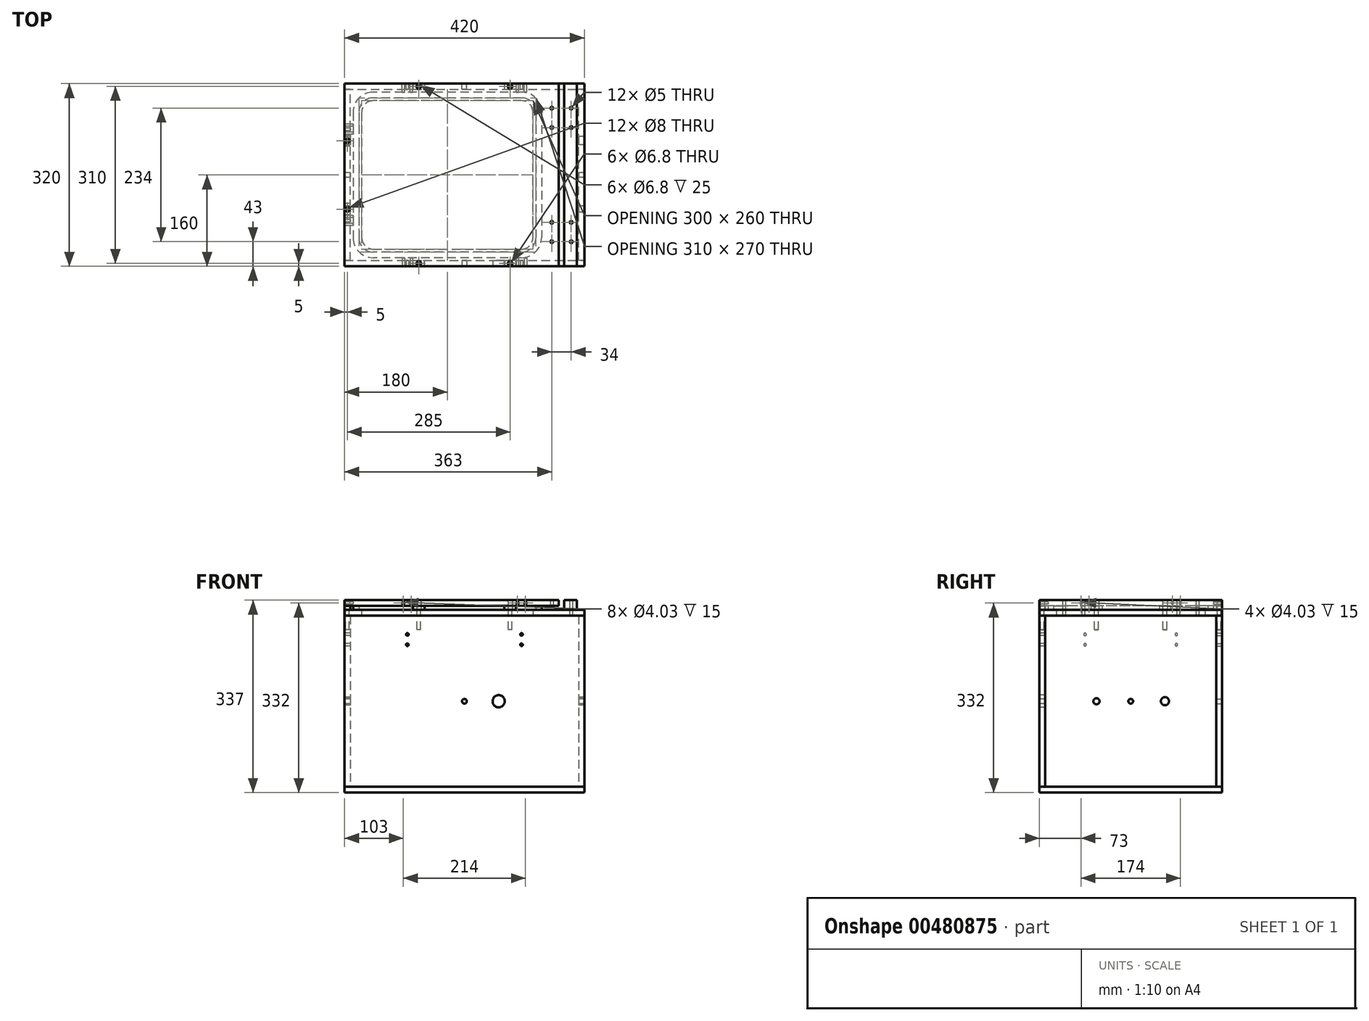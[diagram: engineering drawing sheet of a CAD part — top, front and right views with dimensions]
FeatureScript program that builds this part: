
annotation { "Feature Type Name" : "Feature", "Feature Type Description" : "" }
export const myFeature = defineFeature(function(context is Context, id is Id, definition is map)
    precondition{}
    {
        {
            var Q0;
            Q0=qCreatedBy(makeId("Top.planeOp"),FACE);
            var sketch = newSketch(context, id + "F0", { "sketchPlane" : qUnion([Q0])});
            skLineSegment(sketch, "E0.bottom", {"start": v(-210, 150) * mm, "end": v(210, 150) * mm});
            skLineSegment(sketch, "E0.top", {"start": v(-210, -150) * mm, "end": v(210, -150) * mm});
            skLineSegment(sketch, "E0.left", {"start": v(-200, 150) * mm, "end": v(-200, -150) * mm});
            skLineSegment(sketch, "E0.right", {"start": v(200, 150) * mm, "end": v(200, -150) * mm});
            skLineSegment(sketch, "E1", {"start": v(-200, 0) * mm, "end": v(200, 0) * mm, "construction": true});
            skLineSegment(sketch, "E2", {"start": v(0, -150) * mm, "end": v(0, 150) * mm, "construction": true});
            skLineSegment(sketch, "E3.0", {"start": v(210, 160) * mm, "end": v(210, -160) * mm});
            skLineSegment(sketch, "E3.1", {"start": v(-210, 160) * mm, "end": v(210, 160) * mm});
            skLineSegment(sketch, "E3.2", {"start": v(-210, 160) * mm, "end": v(-210, -160) * mm});
            skLineSegment(sketch, "E3.3", {"start": v(-210, -160) * mm, "end": v(210, -160) * mm});
            skLineSegment(sketch, "E4", {"start": v(-200, 150) * mm, "end": v(-200, 160) * mm, "construction": true});
            skLineSegment(sketch, "E5", {"start": v(-200, -150) * mm, "end": v(-200, -160) * mm, "construction": true});
            skSolve(sketch);
        }
        {
            var Q0;
            Q0=qCreatedBy(makeId("Top.planeOp"),FACE);
            cPlane(context, id + "F1", {"entities" : qUnion([Q0]), "cplaneType" : CPlaneType.OFFSET, "offset" : 150 * mm, "width" : 150 * mm, "height" : 150 * mm});
        }
        {
            var Q0;
            Q0=qCreatedBy(makeId("Top.planeOp"),FACE);
            cPlane(context, id + "F2", {"entities" : qUnion([Q0]), "cplaneType" : CPlaneType.OFFSET, "offset" : 150 * mm, "oppositeDirection" : true, "width" : 150 * mm, "height" : 150 * mm});
        }
        {
            var Q0;
            Q0=qCreatedBy(id+"F2.planeOp",FACE);
            var sketch = newSketch(context, id + "F3", { "sketchPlane" : qUnion([Q0])});
            skLineSegment(sketch, "E6.0", {"start": v(-210, 160) * mm, "end": v(-210, -160) * mm});
            skLineSegment(sketch, "E7.0", {"start": v(-210, 160) * mm, "end": v(210, 160) * mm});
            skLineSegment(sketch, "E8.0", {"start": v(-210, -160) * mm, "end": v(210, -160) * mm});
            skLineSegment(sketch, "E9.0", {"start": v(210, 160) * mm, "end": v(210, -160) * mm});
            skSolve(sketch);
        }
        {
            var Q0;
            Q0=qCreatedBy(id+"F1.planeOp",FACE);
            var sketch = newSketch(context, id + "F4", { "sketchPlane" : qUnion([Q0])});
            skLineSegment(sketch, "E10.0", {"start": v(-210, 160) * mm, "end": v(210, 160) * mm});
            skLineSegment(sketch, "E11.0", {"start": v(-210, 160) * mm, "end": v(-210, -160) * mm});
            skLineSegment(sketch, "E12.0", {"start": v(-210, -160) * mm, "end": v(210, -160) * mm});
            skLineSegment(sketch, "E13.0", {"start": v(210, 160) * mm, "end": v(210, -160) * mm});
            skSolve(sketch);
        }
        {
            var Q0;
            Q0=qCreatedBy(makeId("Right.planeOp"),FACE);
            var Q1;
            Q1=sQuery(id+"F0.wireOp",EDGE,"E0.left");
            cPlane(context, id + "F5", {"entities" : qUnion([Q0, Q1]), "cplaneType" : CPlaneType.LINE_ANGLE, "offset" : 25 * mm, "angle" : 0 * degree, "width" : 150 * mm, "height" : 150 * mm});
        }
        {
            var Q0;
            Q0=qCreatedBy(id+"F5.planeOp",FACE);
            var sketch = newSketch(context, id + "F6", { "sketchPlane" : qUnion([Q0])});
            skLineSegment(sketch, "E14.bottom", {"start": v(-160, 150) * mm, "end": v(160, 150) * mm});
            skLineSegment(sketch, "E14.top", {"start": v(-160, -150) * mm, "end": v(160, -150) * mm});
            skLineSegment(sketch, "E14.left", {"start": v(-160, 150) * mm, "end": v(-160, -150) * mm});
            skLineSegment(sketch, "E14.right", {"start": v(160, 150) * mm, "end": v(160, -150) * mm});
            skPoint(sketch, "E15.0", {"position": v(-160, 0) * mm});
            skPoint(sketch, "E16.0", {"position": v(160, 0) * mm});
            skCircle(sketch, "E17", {"center": v(0, 0) * mm, "radius": 4.17 * mm});
            skCircle(sketch, "E18", {"center": v(60, 0) * mm, "radius": 5.36 * mm});
            skCircle(sketch, "E19", {"center": v(-60, 0) * mm, "radius": 7.13 * mm});
            skSolve(sketch);
        }
        {
            var Q0;
            Q0=makeQuery(id+"F4.imprint","IMPRINT",FACE,{"disambiguationData":[TD([[makeQuery(id+"F4.imprint","IMPRINT",EDGE,{"derivedFrom":sQuery(id+"F4.wireOp",EDGE,"E11.0")}),1.0]])]});
            var sketch = newSketch(context, id + "F7", { "sketchPlane" : qUnion([Q0])});
            skLineSegment(sketch, "E20.0", {"start": v(-210, 160) * mm, "end": v(210, 160) * mm});
            skLineSegment(sketch, "E21.0", {"start": v(210, 160) * mm, "end": v(210, -160) * mm, "construction": true});
            skLineSegment(sketch, "E22.0", {"start": v(-210, -160) * mm, "end": v(210, -160) * mm});
            skLineSegment(sketch, "E23.0", {"start": v(-210, 160) * mm, "end": v(-210, -160) * mm});
            skLineSegment(sketch, "E24.bottom", {"start": v(100, 130) * mm, "end": v(-160, 130) * mm});
            skLineSegment(sketch, "E24.top", {"start": v(100, -130) * mm, "end": v(-160, -130) * mm});
            skLineSegment(sketch, "E24.left", {"start": v(120, 110) * mm, "end": v(120, -110) * mm});
            skLineSegment(sketch, "E24.right", {"start": v(-180, 110) * mm, "end": v(-180, -110) * mm});
            skPoint(sketch, "E25.visualSharp", {"position": v(120, 130) * mm});
            skArc(sketch, "E25.filletArc", {"start": v(120, 110) * mm, "mid": v(114.14, 124.14) * mm, "end": v(100, 130) * mm});
            skPoint(sketch, "E26.visualSharp", {"position": v(-180, 130) * mm});
            skArc(sketch, "E26.filletArc", {"start": v(-160, 130) * mm, "mid": v(-174.14, 124.14) * mm, "end": v(-180, 110) * mm});
            skPoint(sketch, "E27.visualSharp", {"position": v(-180, -130) * mm});
            skArc(sketch, "E27.filletArc", {"start": v(-180, -110) * mm, "mid": v(-174.14, -124.14) * mm, "end": v(-160, -130) * mm});
            skPoint(sketch, "E28.visualSharp", {"position": v(120, -130) * mm});
            skArc(sketch, "E28.filletArc", {"start": v(100, -130) * mm, "mid": v(114.14, -124.14) * mm, "end": v(120, -110) * mm});
            skLineSegment(sketch, "E29.0", {"start": v(100, 135) * mm, "end": v(-160, 135) * mm});
            skArc(sketch, "E29.1", {"start": v(125, 110) * mm, "mid": v(117.68, 127.68) * mm, "end": v(100, 135) * mm});
            skArc(sketch, "E29.2", {"start": v(-160, 135) * mm, "mid": v(-177.68, 127.68) * mm, "end": v(-185, 110) * mm});
            skLineSegment(sketch, "E29.3", {"start": v(125, 110) * mm, "end": v(125, -110) * mm});
            skLineSegment(sketch, "E29.4", {"start": v(-185, 110) * mm, "end": v(-185, -110) * mm});
            skArc(sketch, "E29.5", {"start": v(-185, -110) * mm, "mid": v(-177.68, -127.68) * mm, "end": v(-160, -135) * mm});
            skLineSegment(sketch, "E29.6", {"start": v(100, -135) * mm, "end": v(-160, -135) * mm});
            skArc(sketch, "E29.7", {"start": v(100, -135) * mm, "mid": v(117.68, -127.68) * mm, "end": v(125, -110) * mm});
            skArc(sketch, "E30.0", {"start": v(135, 110) * mm, "mid": v(124.75, 134.75) * mm, "end": v(100, 145) * mm});
            skLineSegment(sketch, "E30.1", {"start": v(135, 110) * mm, "end": v(135, -110) * mm});
            skLineSegment(sketch, "E30.2", {"start": v(100, 145) * mm, "end": v(-160, 145) * mm});
            skArc(sketch, "E30.3", {"start": v(100, -145) * mm, "mid": v(124.75, -134.75) * mm, "end": v(135, -110) * mm});
            skArc(sketch, "E30.4", {"start": v(-160, 145) * mm, "mid": v(-184.75, 134.75) * mm, "end": v(-195, 110) * mm});
            skLineSegment(sketch, "E30.5", {"start": v(-195, 110) * mm, "end": v(-195, -110) * mm});
            skArc(sketch, "E30.6", {"start": v(-195, -110) * mm, "mid": v(-184.75, -134.75) * mm, "end": v(-160, -145) * mm});
            skLineSegment(sketch, "E30.7", {"start": v(100, -145) * mm, "end": v(-160, -145) * mm});
            skLineSegment(sketch, "E31.bottom", {"start": v(153, 117) * mm, "end": v(187, 117) * mm, "construction": true});
            skLineSegment(sketch, "E31.top", {"start": v(153, 83) * mm, "end": v(187, 83) * mm, "construction": true});
            skLineSegment(sketch, "E31.left", {"start": v(153, 117) * mm, "end": v(153, 83) * mm, "construction": true});
            skLineSegment(sketch, "E31.right", {"start": v(187, 117) * mm, "end": v(187, 83) * mm, "construction": true});
            skLineSegment(sketch, "E32", {"start": v(153, 100) * mm, "end": v(187, 100) * mm, "construction": true});
            skLineSegment(sketch, "E33", {"start": v(170, 83) * mm, "end": v(170, 117) * mm, "construction": true});
            skCircle(sketch, "E34", {"center": v(187, 117) * mm, "radius": 2.5 * mm, "construction": true});
            skCircle(sketch, "E35", {"center": v(153, 117) * mm, "radius": 2.5 * mm, "construction": true});
            skCircle(sketch, "E36", {"center": v(153, 83) * mm, "radius": 2.5 * mm, "construction": true});
            skCircle(sketch, "E37", {"center": v(187, 83) * mm, "radius": 2.5 * mm, "construction": true});
            skLineSegment(sketch, "E38", {"start": v(210, 0) * mm, "end": v(-210, 0) * mm, "construction": true});
            skCircle(sketch, "E39.MirrorC", {"center": v(153, -83) * mm, "radius": 2.5 * mm, "construction": true});
            skCircle(sketch, "E40.MirrorC", {"center": v(187, -83) * mm, "radius": 2.5 * mm, "construction": true});
            skCircle(sketch, "E41.MirrorC", {"center": v(153, -117) * mm, "radius": 2.5 * mm, "construction": true});
            skCircle(sketch, "E42.MirrorC", {"center": v(187, -117) * mm, "radius": 2.5 * mm, "construction": true});
            skLineSegment(sketch, "E43.MirrorCS", {"start": v(153, -100) * mm, "end": v(187, -100) * mm, "construction": true});
            skLineSegment(sketch, "E44.MirrorCS", {"start": v(153, -83) * mm, "end": v(187, -83) * mm, "construction": true});
            skLineSegment(sketch, "E45.MirrorCS", {"start": v(170, -83) * mm, "end": v(170, -117) * mm, "construction": true});
            skLineSegment(sketch, "E46.MirrorCS", {"start": v(153, -117) * mm, "end": v(187, -117) * mm, "construction": true});
            skLineSegment(sketch, "E47.MirrorCS", {"start": v(187, -117) * mm, "end": v(187, -83) * mm, "construction": true});
            skLineSegment(sketch, "E48.MirrorCS", {"start": v(153, -117) * mm, "end": v(153, -83) * mm, "construction": true});
            skLineSegment(sketch, "E49", {"start": v(210, -160) * mm, "end": v(210, -160) * mm});
            skLineSegment(sketch, "E50", {"start": v(210, -160) * mm, "end": v(210, 160) * mm});
            skLineSegment(sketch, "E51", {"start": v(210, 160) * mm, "end": v(210, 160) * mm});
            skCircle(sketch, "E52", {"center": v(-205, -60) * mm, "radius": 3.4 * mm});
            skCircle(sketch, "E53", {"center": v(-80, -155) * mm, "radius": 3.4 * mm});
            skCircle(sketch, "E54", {"center": v(80, -155) * mm, "radius": 3.4 * mm});
            skCircle(sketch, "E55.MirrorC", {"center": v(-205, 60) * mm, "radius": 3.4 * mm});
            skCircle(sketch, "E56.MirrorC", {"center": v(-80, 155) * mm, "radius": 3.4 * mm});
            skCircle(sketch, "E57.MirrorC", {"center": v(80, 155) * mm, "radius": 3.4 * mm});
            skSolve(sketch);
        }
        {
            var Q0;
            Q0=qCreatedBy(id+"F1.planeOp",FACE);
            cPlane(context, id + "F8", {"entities" : qUnion([Q0]), "cplaneType" : CPlaneType.OFFSET, "offset" : 10 * mm, "width" : 150 * mm, "height" : 150 * mm});
        }
        {
            var Q0;
            Q0=qCreatedBy(id+"F1.planeOp",FACE);
            var sketch = newSketch(context, id + "F9", { "sketchPlane" : qUnion([Q0])});
            skLineSegment(sketch, "E58.0", {"start": v(-210, 160) * mm, "end": v(210, 160) * mm});
            skLineSegment(sketch, "E59.0", {"start": v(-210, 160) * mm, "end": v(-210, -160) * mm});
            skLineSegment(sketch, "E60.0", {"start": v(-210, -160) * mm, "end": v(210, -160) * mm});
            skLineSegment(sketch, "E61.0.0", {"start": v(-160, -130) * mm, "end": v(100, -130) * mm});
            skArc(sketch, "E61.0.1", {"start": v(100, -130) * mm, "mid": v(114.14, -124.14) * mm, "end": v(120, -110) * mm});
            skLineSegment(sketch, "E61.0.2", {"start": v(120, -110) * mm, "end": v(120, 110) * mm});
            skArc(sketch, "E61.0.3", {"start": v(120, 110) * mm, "mid": v(114.14, 124.14) * mm, "end": v(100, 130) * mm});
            skLineSegment(sketch, "E61.0.4", {"start": v(100, 130) * mm, "end": v(-160, 130) * mm});
            skArc(sketch, "E61.0.5", {"start": v(-160, 130) * mm, "mid": v(-174.14, 124.14) * mm, "end": v(-180, 110) * mm});
            skLineSegment(sketch, "E61.0.6", {"start": v(-180, 110) * mm, "end": v(-180, -110) * mm});
            skArc(sketch, "E61.0.7", {"start": v(-180, -110) * mm, "mid": v(-174.14, -124.14) * mm, "end": v(-160, -130) * mm});
            skLineSegment(sketch, "E62.0", {"start": v(210, -160) * mm, "end": v(210, 160) * mm});
            skSolve(sketch);
        }
        {
            var Q0;
            Q0=qCreatedBy(id+"F8.planeOp",FACE);
            cPlane(context, id + "F10", {"entities" : qUnion([Q0]), "cplaneType" : CPlaneType.OFFSET, "offset" : 7 * mm, "width" : 150 * mm, "height" : 150 * mm});
        }
        {
            var Q0;
            Q0=qCreatedBy(id+"F10.planeOp",FACE);
            var sketch = newSketch(context, id + "F11", { "sketchPlane" : qUnion([Q0])});
            skLineSegment(sketch, "E63.bottom", {"start": v(-210, 160) * mm, "end": v(165, 160) * mm});
            skLineSegment(sketch, "E63.top", {"start": v(-210, -160) * mm, "end": v(165, -160) * mm});
            skLineSegment(sketch, "E63.left", {"start": v(-210, 160) * mm, "end": v(-210, -160) * mm});
            skLineSegment(sketch, "E63.right", {"start": v(165, 160) * mm, "end": v(165, -160) * mm});
            skCircle(sketch, "E64.0", {"center": v(153, 83) * mm, "radius": 2.5 * mm});
            skCircle(sketch, "E65.0", {"center": v(153, 117) * mm, "radius": 2.5 * mm});
            skCircle(sketch, "E66.0", {"center": v(153, -117) * mm, "radius": 2.5 * mm});
            skCircle(sketch, "E67.0", {"center": v(153, -83) * mm, "radius": 2.5 * mm});
            skSolve(sketch);
        }
        {
            var Q0;
            Q0=qCreatedBy(id+"F8.planeOp",FACE);
            var sketch = newSketch(context, id + "F12", { "sketchPlane" : qUnion([Q0])});
            skLineSegment(sketch, "E68.bottom", {"start": v(175, 160) * mm, "end": v(197, 160) * mm});
            skLineSegment(sketch, "E68.top", {"start": v(175, -160) * mm, "end": v(197, -160) * mm});
            skLineSegment(sketch, "E68.left", {"start": v(175, 160) * mm, "end": v(175, -160) * mm});
            skLineSegment(sketch, "E68.right", {"start": v(197, 160) * mm, "end": v(197, -160) * mm});
            skCircle(sketch, "E69", {"center": v(186, 50) * mm, "radius": 4 * mm});
            skCircle(sketch, "E70", {"center": v(186, -50) * mm, "radius": 4 * mm});
            skLineSegment(sketch, "E71", {"start": v(186, -160) * mm, "end": v(186, 160) * mm, "construction": true});
            skSolve(sketch);
        }
        {
            var Q0;
            Q0=qCreatedBy(id+"F5.planeOp",FACE);
            cPlane(context, id + "F13", {"entities" : qUnion([Q0]), "cplaneType" : CPlaneType.OFFSET, "offset" : 10 * mm, "width" : 150 * mm, "height" : 150 * mm});
        }
        {
            var Q0;
            Q0=qCreatedBy(id+"F13.planeOp",FACE);
            var sketch = newSketch(context, id + "F14", { "sketchPlane" : qUnion([Q0])});
            skPoint(sketch, "E72.0", {"position": v(160, 0) * mm});
            skPoint(sketch, "E73.0", {"position": v(-160, 0) * mm});
            skPoint(sketch, "E74.0", {"position": v(-160, 167) * mm});
            skPoint(sketch, "E75.0", {"position": v(160, 167) * mm});
            skLineSegment(sketch, "E76.bottom", {"start": v(-160, 177) * mm, "end": v(160, 177) * mm, "construction": true});
            skLineSegment(sketch, "E76.top", {"start": v(-160, 167) * mm, "end": v(160, 167) * mm, "construction": true});
            skLineSegment(sketch, "E76.left", {"start": v(-160, 177) * mm, "end": v(-160, 167) * mm, "construction": true});
            skLineSegment(sketch, "E76.right", {"start": v(160, 177) * mm, "end": v(160, 167) * mm, "construction": true});
            skLineSegment(sketch, "E77", {"start": v(0, -151.17) * mm, "end": v(0, 177) * mm, "construction": true});
            skCircle(sketch, "E78", {"center": v(73, 172) * mm, "radius": 2.02 * mm});
            skCircle(sketch, "E79", {"center": v(87, 172) * mm, "radius": 2.02 * mm});
            skLineSegment(sketch, "E80", {"start": v(73, 172) * mm, "end": v(87, 172) * mm, "construction": true});
            skPoint(sketch, "E81", {"position": v(80, 172) * mm});
            skLineSegment(sketch, "E82", {"start": v(80, 172) * mm, "end": v(80, 117) * mm});
            skCircle(sketch, "E83", {"center": v(80, 117) * mm, "radius": 2.25 * mm});
            skCircle(sketch, "E84", {"center": v(80, 99) * mm, "radius": 2.25 * mm});
            skLineSegment(sketch, "E85.bottom", {"start": v(71.5, 123) * mm, "end": v(88.5, 123) * mm});
            skLineSegment(sketch, "E85.top", {"start": v(71.5, 93) * mm, "end": v(88.5, 93) * mm});
            skLineSegment(sketch, "E85.left", {"start": v(71.5, 123) * mm, "end": v(71.5, 93) * mm});
            skLineSegment(sketch, "E85.right", {"start": v(88.5, 123) * mm, "end": v(88.5, 93) * mm});
            skPoint(sketch, "E86.MirrorP", {"position": v(-80, 172) * mm});
            skLineSegment(sketch, "E87.MirrorCS", {"start": v(-73, 172) * mm, "end": v(-87, 172) * mm, "construction": true});
            skCircle(sketch, "E88.MirrorC", {"center": v(-80, 117) * mm, "radius": 2.25 * mm});
            skLineSegment(sketch, "E89.MirrorCS", {"start": v(-71.5, 93) * mm, "end": v(-88.5, 93) * mm});
            skLineSegment(sketch, "E90.MirrorCS", {"start": v(-88.5, 123) * mm, "end": v(-88.5, 93) * mm});
            skLineSegment(sketch, "E91.MirrorCS", {"start": v(-80, 172) * mm, "end": v(-80, 117) * mm});
            skCircle(sketch, "E92.MirrorC", {"center": v(-80, 99) * mm, "radius": 2.25 * mm});
            skLineSegment(sketch, "E93.MirrorCS", {"start": v(-71.5, 123) * mm, "end": v(-88.5, 123) * mm});
            skLineSegment(sketch, "E94.MirrorCS", {"start": v(-71.5, 123) * mm, "end": v(-71.5, 93) * mm});
            skCircle(sketch, "E95.MirrorC", {"center": v(-87, 172) * mm, "radius": 2.02 * mm});
            skCircle(sketch, "E96.MirrorC", {"center": v(-73, 172) * mm, "radius": 2.02 * mm});
            skSolve(sketch);
        }
        {
            var Q0;
            Q0=qCreatedBy(makeId("Front.planeOp"),FACE);
            var Q1;
            Q1=sQuery(id+"F0.wireOp",EDGE,"E3.3");
            cPlane(context, id + "F15", {"entities" : qUnion([Q0, Q1]), "cplaneType" : CPlaneType.LINE_ANGLE, "offset" : 25 * mm, "angle" : 0 * degree, "width" : 150 * mm, "height" : 150 * mm});
        }
        {
            var Q0;
            Q0=qCreatedBy(id+"F15.planeOp",FACE);
            var sketch = newSketch(context, id + "F16", { "sketchPlane" : qUnion([Q0])});
            skPoint(sketch, "E97.0", {"position": v(210, 0) * mm});
            skPoint(sketch, "E98.0", {"position": v(-210, 0) * mm});
            skLineSegment(sketch, "E99.bottom", {"start": v(210, 150) * mm, "end": v(-210, 150) * mm});
            skLineSegment(sketch, "E99.top", {"start": v(210, -150) * mm, "end": v(-210, -150) * mm});
            skLineSegment(sketch, "E99.left", {"start": v(210, 150) * mm, "end": v(210, -150) * mm});
            skLineSegment(sketch, "E99.right", {"start": v(-210, 150) * mm, "end": v(-210, -150) * mm});
            skPoint(sketch, "E100.0", {"position": v(210, -150) * mm});
            skPoint(sketch, "E101.0", {"position": v(210, 167) * mm});
            skPoint(sketch, "E102.0", {"position": v(-165, 167) * mm});
            skLineSegment(sketch, "E103.top", {"start": v(210, 167) * mm, "end": v(-165, 167) * mm});
            skLineSegment(sketch, "E103.left", {"start": v(210, 177) * mm, "end": v(210, 167) * mm});
            skCircle(sketch, "E104", {"center": v(107, 172) * mm, "radius": 2.02 * mm});
            skCircle(sketch, "E105", {"center": v(93, 172) * mm, "radius": 2.02 * mm});
            skLineSegment(sketch, "E106", {"start": v(107, 172) * mm, "end": v(93, 172) * mm, "construction": true});
            skPoint(sketch, "E107", {"position": v(100, 172) * mm});
            skLineSegment(sketch, "E108", {"start": v(100, 172) * mm, "end": v(100, 117) * mm, "construction": true});
            skCircle(sketch, "E109", {"center": v(100, 117) * mm, "radius": 2.25 * mm});
            skCircle(sketch, "E110", {"center": v(100, 99) * mm, "radius": 2.25 * mm});
            skLineSegment(sketch, "E111", {"start": v(0, -150) * mm, "end": v(0, 150) * mm, "construction": true});
            skCircle(sketch, "E112.MirrorC", {"center": v(-100, 117) * mm, "radius": 2.25 * mm});
            skCircle(sketch, "E113.MirrorC", {"center": v(-100, 99) * mm, "radius": 2.25 * mm});
            skLineSegment(sketch, "E114.MirrorCS", {"start": v(-100, 172) * mm, "end": v(-100, 117) * mm, "construction": true});
            skCircle(sketch, "E115.MirrorC", {"center": v(-107, 172) * mm, "radius": 2.02 * mm});
            skLineSegment(sketch, "E116.MirrorCS", {"start": v(-107, 172) * mm, "end": v(-93, 172) * mm, "construction": true});
            skPoint(sketch, "E117.MirrorP", {"position": v(-100, 172) * mm});
            skCircle(sketch, "E118.MirrorC", {"center": v(-93, 172) * mm, "radius": 2.02 * mm});
            skLineSegment(sketch, "E119", {"start": v(210, 177) * mm, "end": v(-165, 177) * mm});
            skLineSegment(sketch, "E120", {"start": v(-165, 167) * mm, "end": v(-165, 177) * mm});
            skCircle(sketch, "E121", {"center": v(-60, 0) * mm, "radius": 10.67 * mm});
            skCircle(sketch, "E122", {"center": v(0, 0) * mm, "radius": 4.17 * mm});
            skSolve(sketch);
        }
        {
            var Q0;
            Q0=qCreatedBy(id+"F1.planeOp",FACE);
            var sketch = newSketch(context, id + "F17", { "sketchPlane" : qUnion([Q0])});
            skPoint(sketch, "E123.0", {"position": v(80, -155) * mm});
            skPoint(sketch, "E124.0", {"position": v(-80, -155) * mm});
            skPoint(sketch, "E125.0", {"position": v(-205, -60) * mm});
            skCircle(sketch, "E126", {"center": v(-205, -60) * mm, "radius": 4 * mm});
            skCircle(sketch, "E127", {"center": v(-80, -155) * mm, "radius": 4 * mm});
            skCircle(sketch, "E128", {"center": v(80, -155) * mm, "radius": 4 * mm});
            skCircle(sketch, "E129.MirrorC", {"center": v(-80, 155) * mm, "radius": 4 * mm});
            skCircle(sketch, "E130.MirrorC", {"center": v(-205, 60) * mm, "radius": 4 * mm});
            skCircle(sketch, "E131.MirrorC", {"center": v(80, 155) * mm, "radius": 4 * mm});
            skSolve(sketch);
        }
        {
            var Q0;
            Q0=qCreatedBy(id+"F8.planeOp",FACE);
            var sketch = newSketch(context, id + "F18", { "sketchPlane" : qUnion([Q0])});
            skLineSegment(sketch, "E132.bottom", {"start": v(-70, -160) * mm, "end": v(-90, -160) * mm});
            skLineSegment(sketch, "E132.top", {"start": v(-70, -150) * mm, "end": v(-90, -150) * mm});
            skLineSegment(sketch, "E132.left", {"start": v(-70, -160) * mm, "end": v(-70, -150) * mm});
            skLineSegment(sketch, "E132.right", {"start": v(-90, -160) * mm, "end": v(-90, -150) * mm});
            skLineSegment(sketch, "E133", {"start": v(-80, -150) * mm, "end": v(-80, -160) * mm, "construction": true});
            skCircle(sketch, "E134.0", {"center": v(-80, -155) * mm, "radius": 4 * mm});
            skLineSegment(sketch, "E135.1.0.0", {"start": v(90, -160) * mm, "end": v(90, -150) * mm});
            skCircle(sketch, "E135.1.0.1", {"center": v(80, -155) * mm, "radius": 4 * mm});
            skLineSegment(sketch, "E135.1.0.2", {"start": v(80, -150) * mm, "end": v(80, -160) * mm, "construction": true});
            skLineSegment(sketch, "E135.1.0.3", {"start": v(70, -160) * mm, "end": v(70, -150) * mm});
            skLineSegment(sketch, "E135.1.0.4", {"start": v(90, -160) * mm, "end": v(70, -160) * mm});
            skLineSegment(sketch, "E135.1.0.5", {"start": v(90, -150) * mm, "end": v(70, -150) * mm});
            skLineSegment(sketch, "E135.direction1", {"start": v(-90, -160) * mm, "end": v(70, -160) * mm, "construction": true});
            skLineSegment(sketch, "E136.bottom", {"start": v(-200, -70) * mm, "end": v(-210, -70) * mm});
            skLineSegment(sketch, "E136.top", {"start": v(-200, -50) * mm, "end": v(-210, -50) * mm});
            skLineSegment(sketch, "E136.left", {"start": v(-200, -70) * mm, "end": v(-200, -50) * mm});
            skLineSegment(sketch, "E136.right", {"start": v(-210, -70) * mm, "end": v(-210, -50) * mm});
            skLineSegment(sketch, "E137", {"start": v(-200, -60) * mm, "end": v(-210, -60) * mm, "construction": true});
            skCircle(sketch, "E138.0", {"center": v(-205, -60) * mm, "radius": 4 * mm});
            skLineSegment(sketch, "E139.MirrorCS", {"start": v(-200, 60) * mm, "end": v(-210, 60) * mm, "construction": true});
            skLineSegment(sketch, "E140.MirrorCS", {"start": v(-200, 50) * mm, "end": v(-210, 50) * mm});
            skLineSegment(sketch, "E141.MirrorCS", {"start": v(-200, 70) * mm, "end": v(-210, 70) * mm});
            skLineSegment(sketch, "E142.MirrorCS", {"start": v(-210, 70) * mm, "end": v(-210, 50) * mm});
            skLineSegment(sketch, "E143.MirrorCS", {"start": v(-200, 70) * mm, "end": v(-200, 50) * mm});
            skCircle(sketch, "E144.MirrorC", {"center": v(-205, 60) * mm, "radius": 4 * mm});
            skLineSegment(sketch, "E145.MirrorCS", {"start": v(-80, 150) * mm, "end": v(-80, 160) * mm, "construction": true});
            skLineSegment(sketch, "E146.MirrorCS", {"start": v(-90, 160) * mm, "end": v(-90, 150) * mm});
            skLineSegment(sketch, "E147.MirrorCS", {"start": v(-70, 160) * mm, "end": v(-70, 150) * mm});
            skCircle(sketch, "E148.MirrorC", {"center": v(-80, 155) * mm, "radius": 4 * mm});
            skLineSegment(sketch, "E149.MirrorCS", {"start": v(-70, 150) * mm, "end": v(-90, 150) * mm});
            skLineSegment(sketch, "E150.MirrorCS", {"start": v(-70, 160) * mm, "end": v(-90, 160) * mm});
            skLineSegment(sketch, "E151.MirrorCS", {"start": v(80, 150) * mm, "end": v(80, 160) * mm, "construction": true});
            skLineSegment(sketch, "E152.MirrorCS", {"start": v(90, 160) * mm, "end": v(70, 160) * mm});
            skLineSegment(sketch, "E153.MirrorCS", {"start": v(90, 160) * mm, "end": v(90, 150) * mm});
            skCircle(sketch, "E154.MirrorC", {"center": v(80, 155) * mm, "radius": 4 * mm});
            skLineSegment(sketch, "E155.MirrorCS", {"start": v(70, 160) * mm, "end": v(70, 150) * mm});
            skLineSegment(sketch, "E156.MirrorCS", {"start": v(90, 150) * mm, "end": v(70, 150) * mm});
            skSolve(sketch);
        }
        {
            var Q0;
            Q0 = qSketchRegion(id + "F9", true);
            extrude(context, id + "F19", {"entities" : qUnion([Q0]), "depth" : 10 * mm});
        }
        {
            var Q0;
            Q0=qCreatedBy(id+"F1.planeOp",FACE);
            var sketch = newSketch(context, id + "F20", { "sketchPlane" : qUnion([Q0])});
            skCircle(sketch, "E157.0", {"center": v(187, 83) * mm, "radius": 2.5 * mm});
            skCircle(sketch, "E158.0", {"center": v(187, 117) * mm, "radius": 2.5 * mm});
            skCircle(sketch, "E159.0", {"center": v(187, -83) * mm, "radius": 2.5 * mm});
            skCircle(sketch, "E160.0", {"center": v(187, -117) * mm, "radius": 2.5 * mm});
            skSolve(sketch);
        }
        {
            var Q0;
            Q0 = qSketchRegion(id + "F20", true);
            extrude(context, id + "F21", {"entities" : qUnion([Q0]), "operationType" : NewBodyOperationType.REMOVE, "depth" : 25 * mm});
        }
        {
            var Q0;
            Q0=qCreatedBy(id+"F1.planeOp",FACE);
            var sketch = newSketch(context, id + "F22", { "sketchPlane" : qUnion([Q0])});
            skCircle(sketch, "E161.0", {"center": v(153, 117) * mm, "radius": 2.5 * mm});
            skCircle(sketch, "E162.0", {"center": v(153, 83) * mm, "radius": 2.5 * mm});
            skCircle(sketch, "E163.0", {"center": v(187, 83) * mm, "radius": 2.5 * mm});
            skPoint(sketch, "E164.0", {"position": v(187, 117) * mm});
            skCircle(sketch, "E165.0", {"center": v(187, 117) * mm, "radius": 2.5 * mm});
            skCircle(sketch, "E166.0", {"center": v(153, -83) * mm, "radius": 2.5 * mm});
            skCircle(sketch, "E167.0", {"center": v(187, -83) * mm, "radius": 2.5 * mm});
            skCircle(sketch, "E168.0", {"center": v(187, -117) * mm, "radius": 2.5 * mm});
            skCircle(sketch, "E169.0", {"center": v(153, -117) * mm, "radius": 2.5 * mm});
            skSolve(sketch);
        }
        {
            var Q0;
            Q0=qCreatedBy(id+"F8.planeOp",FACE);
            var sketch = newSketch(context, id + "F23", { "sketchPlane" : qUnion([Q0])});
            skLineSegment(sketch, "E170.0", {"start": v(-195, 110) * mm, "end": v(-195, -110) * mm});
            skLineSegment(sketch, "E171.0", {"start": v(-185, 110) * mm, "end": v(-185, -110) * mm});
            skArc(sketch, "E172.0", {"start": v(-160, 145) * mm, "mid": v(-184.75, 134.75) * mm, "end": v(-195, 110) * mm});
            skArc(sketch, "E173.0", {"start": v(-160, 135) * mm, "mid": v(-177.68, 127.68) * mm, "end": v(-185, 110) * mm});
            skLineSegment(sketch, "E174.0", {"start": v(100, 135) * mm, "end": v(-160, 135) * mm});
            skLineSegment(sketch, "E175.0", {"start": v(100, 145) * mm, "end": v(-160, 145) * mm});
            skPoint(sketch, "E176.0", {"position": v(124.75, 134.75) * mm});
            skArc(sketch, "E177.0", {"start": v(135, 110) * mm, "mid": v(124.75, 134.75) * mm, "end": v(100, 145) * mm});
            skArc(sketch, "E178.0", {"start": v(125, 110) * mm, "mid": v(117.68, 127.68) * mm, "end": v(100, 135) * mm});
            skLineSegment(sketch, "E179.0", {"start": v(135, 110) * mm, "end": v(135, -110) * mm});
            skLineSegment(sketch, "E180.0", {"start": v(125, 110) * mm, "end": v(125, -110) * mm});
            skArc(sketch, "E181.0", {"start": v(100, -135) * mm, "mid": v(117.68, -127.68) * mm, "end": v(125, -110) * mm});
            skArc(sketch, "E182.0", {"start": v(100, -145) * mm, "mid": v(124.75, -134.75) * mm, "end": v(135, -110) * mm});
            skLineSegment(sketch, "E183.0", {"start": v(100, -145) * mm, "end": v(-160, -145) * mm});
            skLineSegment(sketch, "E183.1", {"start": v(100, -135) * mm, "end": v(-160, -135) * mm});
            skArc(sketch, "E184.0", {"start": v(-195, -110) * mm, "mid": v(-184.75, -134.75) * mm, "end": v(-160, -145) * mm});
            skArc(sketch, "E184.1", {"start": v(-185, -110) * mm, "mid": v(-177.68, -127.68) * mm, "end": v(-160, -135) * mm});
            skSolve(sketch);
        }
        {
            var Q0;
            Q0 = qSketchRegion(id + "F23", true);
            extrude(context, id + "F24", {"entities" : qUnion([Q0]), "depth" : 7 * mm});
        }
        {
            var Q0;
            Q0 = qSketchRegion(id + "F11", true);
            extrude(context, id + "F25", {"entities" : qUnion([Q0]), "depth" : 10 * mm});
        }
        {
            var Q0;
            Q0=qCreatedBy(id+"F8.planeOp",FACE);
            var sketch = newSketch(context, id + "F26", { "sketchPlane" : qUnion([Q0])});
            skLineSegment(sketch, "E185.0", {"start": v(175, 160) * mm, "end": v(175, -160) * mm});
            skPoint(sketch, "E186.0", {"position": v(186, 160) * mm});
            skLineSegment(sketch, "E187.0", {"start": v(197, 160) * mm, "end": v(197, -160) * mm});
            skLineSegment(sketch, "E188.0", {"start": v(175, 160) * mm, "end": v(197, 160) * mm});
            skLineSegment(sketch, "E189.0", {"start": v(175, -160) * mm, "end": v(197, -160) * mm});
            skCircle(sketch, "E190.0", {"center": v(187, 117) * mm, "radius": 2.5 * mm});
            skCircle(sketch, "E191.0", {"center": v(187, 83) * mm, "radius": 2.5 * mm});
            skCircle(sketch, "E192.0", {"center": v(187, -83) * mm, "radius": 2.5 * mm});
            skCircle(sketch, "E193.0", {"center": v(187, -117) * mm, "radius": 2.5 * mm});
            skSolve(sketch);
        }
        {
            var Q0;
            Q0 = qSketchRegion(id + "F26", true);
            extrude(context, id + "F27", {"entities" : qUnion([Q0]), "depth" : 17 * mm});
        }
        {
            var Q0;
            Q0=qCreatedBy(id+"F8.planeOp",FACE);
            var sketch = newSketch(context, id + "F28", { "sketchPlane" : qUnion([Q0])});
            skCircle(sketch, "E194.0", {"center": v(-80, -155) * mm, "radius": 3.4 * mm});
            skCircle(sketch, "E195.0", {"center": v(80, -155) * mm, "radius": 3.4 * mm});
            skCircle(sketch, "E196.0", {"center": v(-205, -60) * mm, "radius": 3.4 * mm});
            skCircle(sketch, "E197.0", {"center": v(-205, 60) * mm, "radius": 3.4 * mm});
            skCircle(sketch, "E198.0", {"center": v(-80, 155) * mm, "radius": 3.4 * mm});
            skCircle(sketch, "E199.0", {"center": v(80, 155) * mm, "radius": 3.4 * mm});
            skSolve(sketch);
        }
        {
            var Q0;
            Q0 = qSketchRegion(id + "F28", true);
            extrude(context, id + "F29", {"entities" : qUnion([Q0]), "operationType" : NewBodyOperationType.REMOVE, "oppositeDirection" : true, "depth" : 10 * mm});
        }
        {
            var Q0;
            Q0=qCreatedBy(id+"F10.planeOp",FACE);
            var sketch = newSketch(context, id + "F30", { "sketchPlane" : qUnion([Q0])});
            skCircle(sketch, "E200.0", {"center": v(-80, -155) * mm, "radius": 4 * mm});
            skCircle(sketch, "E201.0", {"center": v(80, -155) * mm, "radius": 4 * mm});
            skCircle(sketch, "E202.0", {"center": v(-205, -60) * mm, "radius": 4 * mm});
            skCircle(sketch, "E203.0", {"center": v(-205, 60) * mm, "radius": 4 * mm});
            skCircle(sketch, "E204.0", {"center": v(-80, 155) * mm, "radius": 4 * mm});
            skCircle(sketch, "E205.0", {"center": v(80, 155) * mm, "radius": 4 * mm});
            skSolve(sketch);
        }
        {
            var Q0;
            Q0 = qSketchRegion(id + "F30", true);
            extrude(context, id + "F31", {"entities" : qUnion([Q0]), "operationType" : NewBodyOperationType.REMOVE, "depth" : 10 * mm});
        }
        {
            var Q0;
            Q0=qCreatedBy(id+"F8.planeOp",FACE);
            var sketch = newSketch(context, id + "F32", { "sketchPlane" : qUnion([Q0])});
            skLineSegment(sketch, "E206.0", {"start": v(90, -150) * mm, "end": v(70, -150) * mm});
            skLineSegment(sketch, "E207.0", {"start": v(70, -160) * mm, "end": v(70, -150) * mm});
            skLineSegment(sketch, "E208.0", {"start": v(90, -160) * mm, "end": v(70, -160) * mm});
            skLineSegment(sketch, "E209.0", {"start": v(90, -160) * mm, "end": v(90, -150) * mm});
            skCircle(sketch, "E210.0", {"center": v(80, -155) * mm, "radius": 4 * mm});
            skSolve(sketch);
        }
        {
            var Q0;
            Q0 = qSketchRegion(id + "F32", true);
            extrude(context, id + "F33", {"entities" : qUnion([Q0]), "depth" : 7 * mm});
        }
        {
            var Q0;
            Q0=makeQuery(id+"F33.opExtrude","SWEPT_BODY",BODY,{"disambiguationData":[OSD([sQuery(id+"F32.wireOp",EDGE,"E206.0"),sQuery(id+"F32.wireOp",EDGE,"E207.0"),sQuery(id+"F32.wireOp",EDGE,"E208.0"),sQuery(id+"F32.wireOp",EDGE,"E209.0"),sQuery(id+"F32.wireOp",EDGE,"E210.0")])]});
            var Q1;
            Q1=qCreatedBy(makeId("Front.planeOp"),FACE);
            mirror(context, id + "F34", {"entities" : qUnion([Q0]), "mirrorPlane" : qUnion([Q1])});
        }
        {
            var Q0;
            Q0=makeQuery(id+"F34.opPattern","COPY",BODY,{"derivedFrom":makeQuery(id+"F33.opExtrude","SWEPT_BODY",BODY,{"disambiguationData":[OSD([sQuery(id+"F32.wireOp",EDGE,"E206.0"),sQuery(id+"F32.wireOp",EDGE,"E207.0"),sQuery(id+"F32.wireOp",EDGE,"E208.0"),sQuery(id+"F32.wireOp",EDGE,"E209.0"),sQuery(id+"F32.wireOp",EDGE,"E210.0")])]}),"instanceName":"1"});
            var Q1;
            Q1=makeQuery(id+"F33.opExtrude","SWEPT_BODY",BODY,{"disambiguationData":[OSD([sQuery(id+"F32.wireOp",EDGE,"E206.0"),sQuery(id+"F32.wireOp",EDGE,"E207.0"),sQuery(id+"F32.wireOp",EDGE,"E208.0"),sQuery(id+"F32.wireOp",EDGE,"E209.0"),sQuery(id+"F32.wireOp",EDGE,"E210.0")])]});
            var Q2;
            Q2=qCreatedBy(makeId("Right.planeOp"),FACE);
            mirror(context, id + "F35", {"entities" : qUnion([Q0, Q1]), "mirrorPlane" : qUnion([Q2])});
        }
        {
            var Q0;
            Q0=qCreatedBy(id+"F8.planeOp",FACE);
            var sketch = newSketch(context, id + "F36", { "sketchPlane" : qUnion([Q0])});
            skLineSegment(sketch, "E211.0", {"start": v(-200, -70) * mm, "end": v(-210, -70) * mm});
            skLineSegment(sketch, "E212.0", {"start": v(-200, -50) * mm, "end": v(-210, -50) * mm});
            skLineSegment(sketch, "E213.0", {"start": v(-200, -70) * mm, "end": v(-200, -50) * mm});
            skLineSegment(sketch, "E214.0", {"start": v(-210, -50) * mm, "end": v(-210, -70) * mm});
            skCircle(sketch, "E215.0", {"center": v(-205, -60) * mm, "radius": 4 * mm});
            skPoint(sketch, "E216.orphan", {"position": v(-210, 160) * mm});
            skPoint(sketch, "E217.orphan", {"position": v(-210, -160) * mm});
            skSolve(sketch);
        }
        {
            var Q0;
            Q0 = qSketchRegion(id + "F36", true);
            extrude(context, id + "F37", {"entities" : qUnion([Q0]), "depth" : 7 * mm});
        }
        {
            var Q0;
            Q0=makeQuery(id+"F37.opExtrude","SWEPT_BODY",BODY,{"disambiguationData":[OSD([sQuery(id+"F36.wireOp",EDGE,"E211.0"),sQuery(id+"F36.wireOp",EDGE,"E212.0"),sQuery(id+"F36.wireOp",EDGE,"E213.0"),sQuery(id+"F36.wireOp",EDGE,"E214.0"),sQuery(id+"F36.wireOp",EDGE,"E215.0")])]});
            var Q1;
            Q1=qCreatedBy(makeId("Front.planeOp"),FACE);
            mirror(context, id + "F38", {"entities" : qUnion([Q0]), "mirrorPlane" : qUnion([Q1])});
        }
        {
            var Q0;
            Q0=makeQuery(id+"F16.imprint","IMPRINT",FACE,{"disambiguationData":[TD([[makeQuery(id+"F16.imprint","IMPRINT",EDGE,{"derivedFrom":sQuery(id+"F16.wireOp",EDGE,"E99.bottom")}),1.0]])]});
            var Q1;
            Q1=makeQuery(id+"F16.imprint","IMPRINT",FACE,{"disambiguationData":[TD([[makeQuery(id+"F16.imprint","IMPRINT",EDGE,{"derivedFrom":sQuery(id+"F16.wireOp",EDGE,"E109")}),1.0]])]});
            var Q2;
            Q2=makeQuery(id+"F16.imprint","IMPRINT",FACE,{"disambiguationData":[TD([[makeQuery(id+"F16.imprint","IMPRINT",EDGE,{"derivedFrom":sQuery(id+"F16.wireOp",EDGE,"E110")}),1.0]])]});
            var Q3;
            Q3=makeQuery(id+"F16.imprint","IMPRINT",FACE,{"disambiguationData":[TD([[makeQuery(id+"F16.imprint","IMPRINT",EDGE,{"derivedFrom":sQuery(id+"F16.wireOp",EDGE,"E112.MirrorC")}),-1.0]])]});
            var Q4;
            Q4=makeQuery(id+"F16.imprint","IMPRINT",FACE,{"disambiguationData":[TD([[makeQuery(id+"F16.imprint","IMPRINT",EDGE,{"derivedFrom":sQuery(id+"F16.wireOp",EDGE,"E113.MirrorC")}),-1.0]])]});
            extrude(context, id + "F39", {"entities" : qUnion([Q0, Q1, Q2, Q3, Q4]), "depth" : 10 * mm});
        }
        {
            var Q0;
            Q0=qCreatedBy(id+"F1.planeOp",FACE);
            var sketch = newSketch(context, id + "F40", { "sketchPlane" : qUnion([Q0])});
            skCircle(sketch, "E218.0", {"center": v(-80, -155) * mm, "radius": 3.4 * mm});
            skCircle(sketch, "E219.0", {"center": v(80, -155) * mm, "radius": 3.4 * mm});
            skSolve(sketch);
        }
        {
            var Q0;
            Q0 = qSketchRegion(id + "F40", true);
            extrude(context, id + "F41", {"entities" : qUnion([Q0]), "operationType" : NewBodyOperationType.REMOVE, "oppositeDirection" : true, "depth" : 25 * mm});
        }
        {
            var Q0;
            Q0=qCreatedBy(id+"F15.planeOp",FACE);
            var sketch = newSketch(context, id + "F42", { "sketchPlane" : qUnion([Q0])});
            skPoint(sketch, "E220.0", {"position": v(100, 117) * mm});
            skCircle(sketch, "E221.0", {"center": v(100, 117) * mm, "radius": 2.25 * mm});
            skCircle(sketch, "E222.0", {"center": v(100, 99) * mm, "radius": 2.25 * mm});
            skCircle(sketch, "E223.0", {"center": v(-100, 117) * mm, "radius": 2.25 * mm});
            skCircle(sketch, "E224.0", {"center": v(-100, 99) * mm, "radius": 2.25 * mm});
            skSolve(sketch);
        }
        {
            var Q0;
            Q0 = qSketchRegion(id + "F42", true);
            extrude(context, id + "F43", {"entities" : qUnion([Q0]), "operationType" : NewBodyOperationType.REMOVE, "depth" : 10 * mm});
        }
        {
            var Q0;
            Q0=makeQuery(id+"F39.opExtrude","SWEPT_BODY",BODY,{"disambiguationData":[OSD([sQuery(id+"F16.wireOp",EDGE,"E99.bottom"),sQuery(id+"F16.wireOp",EDGE,"E99.top"),sQuery(id+"F16.wireOp",EDGE,"E99.left"),sQuery(id+"F16.wireOp",EDGE,"E99.right"),sQuery(id+"F16.wireOp",EDGE,"E121"),sQuery(id+"F16.wireOp",EDGE,"E122")])]});
            var Q1;
            Q1=qCreatedBy(makeId("Front.planeOp"),FACE);
            mirror(context, id + "F44", {"entities" : qUnion([Q0]), "mirrorPlane" : qUnion([Q1])});
        }
        {
            var Q0;
            Q0=makeQuery(id+"F44.opPattern","COPY",FACE,{"derivedFrom":makeQuery(id+"F39.opExtrude","CAP_FACE",FACE,{"disambiguationData":[OSD([sQuery(id+"F16.wireOp",EDGE,"E99.bottom"),sQuery(id+"F16.wireOp",EDGE,"E99.top"),sQuery(id+"F16.wireOp",EDGE,"E99.left"),sQuery(id+"F16.wireOp",EDGE,"E99.right"),sQuery(id+"F16.wireOp",EDGE,"E121"),sQuery(id+"F16.wireOp",EDGE,"E122")])],"isStart":true}),"instanceName":"1"});
            var sketch = newSketch(context, id + "F45", { "sketchPlane" : qUnion([Q0])});
            skCircle(sketch, "E225.0", {"center": v(-60, 0) * mm, "radius": 10.67 * mm});
            skSolve(sketch);
        }
        {
            var Q0;
            Q0 = qSketchRegion(id + "F45", true);
            extrude(context, id + "F46", {"entities" : qUnion([Q0]), "operationType" : NewBodyOperationType.ADD, "oppositeDirection" : true, "depth" : 10 * mm});
        }
        {
            var Q0;
            Q0=qCreatedBy(id+"F15.planeOp",FACE);
            var sketch = newSketch(context, id + "F47", { "sketchPlane" : qUnion([Q0])});
            skCircle(sketch, "E226.0", {"center": v(-93, 172) * mm, "radius": 2.02 * mm});
            skCircle(sketch, "E227.0", {"center": v(-107, 172) * mm, "radius": 2.02 * mm});
            skCircle(sketch, "E228.0", {"center": v(93, 172) * mm, "radius": 2.02 * mm});
            skCircle(sketch, "E229.0", {"center": v(107, 172) * mm, "radius": 2.02 * mm});
            skSolve(sketch);
        }
        {
            var Q0;
            Q0 = qSketchRegion(id + "F47", true);
            extrude(context, id + "F48", {"entities" : qUnion([Q0]), "operationType" : NewBodyOperationType.REMOVE, "depth" : 15 * mm});
        }
        {
            var Q0;
            Q0=qCreatedBy(id+"F13.planeOp",FACE);
            var sketch = newSketch(context, id + "F49", { "sketchPlane" : qUnion([Q0])});
            skCircle(sketch, "E230.0", {"center": v(87, 172) * mm, "radius": 2.02 * mm});
            skPoint(sketch, "E231.0", {"position": v(73, 172) * mm});
            skCircle(sketch, "E232.0", {"center": v(73, 172) * mm, "radius": 2.02 * mm});
            skCircle(sketch, "E233.0", {"center": v(-73, 172) * mm, "radius": 2.02 * mm});
            skCircle(sketch, "E234.0", {"center": v(-87, 172) * mm, "radius": 2.02 * mm});
            skSolve(sketch);
        }
        {
            var Q0;
            Q0 = qSketchRegion(id + "F49", true);
            extrude(context, id + "F50", {"entities" : qUnion([Q0]), "operationType" : NewBodyOperationType.REMOVE, "oppositeDirection" : true, "depth" : 15 * mm});
        }
        {
            var Q0;
            Q0=makeQuery(id+"F25.opExtrude","SWEPT_FACE",FACE,{"disambiguationData":[OSD([sQuery(id+"F11.wireOp",EDGE,"E63.bottom")])]});
            var sketch = newSketch(context, id + "F51", { "sketchPlane" : qUnion([Q0])});
            skPoint(sketch, "E235.0", {"position": v(107, 172) * mm});
            skCircle(sketch, "E236.0", {"center": v(107, 172) * mm, "radius": 2.02 * mm});
            skCircle(sketch, "E237.0", {"center": v(93, 172) * mm, "radius": 2.02 * mm});
            skCircle(sketch, "E238.0", {"center": v(-93, 172) * mm, "radius": 2.02 * mm});
            skCircle(sketch, "E239.0", {"center": v(-107, 172) * mm, "radius": 2.02 * mm});
            skSolve(sketch);
        }
        {
            var Q0;
            Q0 = qSketchRegion(id + "F51", true);
            extrude(context, id + "F52", {"entities" : qUnion([Q0]), "operationType" : NewBodyOperationType.REMOVE, "oppositeDirection" : true, "depth" : 15 * mm});
        }
        {
            var Q0;
            Q0=qCreatedBy(id+"F13.planeOp",FACE);
            var sketch = newSketch(context, id + "F53", { "sketchPlane" : qUnion([Q0])});
            skLineSegment(sketch, "E240.0.1", {"start": v(-150, -150) * mm, "end": v(150, -150) * mm});
            skLineSegment(sketch, "E240.0.3", {"start": v(150, 150) * mm, "end": v(-150, 150) * mm});
            skPoint(sketch, "E241.0", {"position": v(-80, 99) * mm});
            skPoint(sketch, "E242.0", {"position": v(-80, 117) * mm});
            skCircle(sketch, "E243.0", {"center": v(80, 117) * mm, "radius": 2.25 * mm});
            skCircle(sketch, "E244.0", {"center": v(80, 99) * mm, "radius": 2.25 * mm});
            skCircle(sketch, "E245.0", {"center": v(60, 0) * mm, "radius": 5.36 * mm});
            skCircle(sketch, "E246.0", {"center": v(0, 0) * mm, "radius": 4.17 * mm});
            skCircle(sketch, "E247.0", {"center": v(-60, 0) * mm, "radius": 7.13 * mm});
            skCircle(sketch, "E248.0", {"center": v(-80, 117) * mm, "radius": 2.25 * mm});
            skCircle(sketch, "E249.0", {"center": v(-80, 99) * mm, "radius": 2.25 * mm});
            skLineSegment(sketch, "E250.0", {"start": v(-150, 150) * mm, "end": v(-150, -150) * mm});
            skLineSegment(sketch, "E251.0", {"start": v(150, 150) * mm, "end": v(150, -150) * mm});
            skPoint(sketch, "E252.orphan", {"position": v(160, 150) * mm});
            skPoint(sketch, "E253.orphan", {"position": v(-160, 150) * mm});
            skPoint(sketch, "E254.orphan", {"position": v(-160, -150) * mm});
            skPoint(sketch, "E255.orphan", {"position": v(160, -150) * mm});
            skSolve(sketch);
        }
        {
            var Q0;
            Q0 = qSketchRegion(id + "F53", true);
            extrude(context, id + "F54", {"entities" : qUnion([Q0]), "oppositeDirection" : true, "depth" : 10 * mm});
        }
        {
            var Q0;
            Q0=qCreatedBy(id+"F1.planeOp",FACE);
            var sketch = newSketch(context, id + "F55", { "sketchPlane" : qUnion([Q0])});
            skCircle(sketch, "E256.0", {"center": v(-205, 60) * mm, "radius": 3.4 * mm});
            skCircle(sketch, "E257.0", {"center": v(-205, -60) * mm, "radius": 3.4 * mm});
            skSolve(sketch);
        }
        {
            var Q0;
            Q0 = qSketchRegion(id + "F55", true);
            extrude(context, id + "F56", {"entities" : qUnion([Q0]), "operationType" : NewBodyOperationType.REMOVE, "oppositeDirection" : true, "depth" : 25 * mm});
        }
        {
            var Q0;
            Q0=makeQuery(id+"F3.imprint","IMPRINT",FACE,{"disambiguationData":[TD([[makeQuery(id+"F3.imprint","IMPRINT",EDGE,{"derivedFrom":sQuery(id+"F3.wireOp",EDGE,"E6.0")}),1.0]])]});
            var sketch = newSketch(context, id + "F57", { "sketchPlane" : qUnion([Q0])});
            skLineSegment(sketch, "E258.0", {"start": v(-210, 160) * mm, "end": v(210, 160) * mm});
            skLineSegment(sketch, "E259.0", {"start": v(210, 160) * mm, "end": v(210, -160) * mm});
            skLineSegment(sketch, "E260.0", {"start": v(-210, 160) * mm, "end": v(-210, -160) * mm});
            skLineSegment(sketch, "E261.0", {"start": v(-210, -160) * mm, "end": v(210, -160) * mm});
            skSolve(sketch);
        }
        {
            var Q0;
            Q0 = qSketchRegion(id + "F57", true);
            extrude(context, id + "F58", {"entities" : qUnion([Q0]), "oppositeDirection" : true, "depth" : 10 * mm});
        }
        {
            var Q0;
            Q0=qCreatedBy(makeId("Right.planeOp"),FACE);
            var Q1;
            Q1=sQuery(id+"F0.wireOp",EDGE,"E0.right");
            cPlane(context, id + "F59", {"entities" : qUnion([Q0, Q1]), "cplaneType" : CPlaneType.LINE_ANGLE, "offset" : 25 * mm, "angle" : 0 * degree, "width" : 150 * mm, "height" : 150 * mm});
        }
        {
            var Q0;
            Q0=qCreatedBy(id+"F59.planeOp",FACE);
            var sketch = newSketch(context, id + "F60", { "sketchPlane" : qUnion([Q0])});
            skLineSegment(sketch, "E262.0.1", {"start": v(-150, -150) * mm, "end": v(150, -150) * mm});
            skLineSegment(sketch, "E262.0.3", {"start": v(150, 150) * mm, "end": v(-150, 150) * mm});
            skLineSegment(sketch, "E263.0", {"start": v(-150, 150) * mm, "end": v(-150, -150) * mm});
            skLineSegment(sketch, "E264.0", {"start": v(150, 150) * mm, "end": v(150, -150) * mm});
            skPoint(sketch, "E262.0.2.end.orphan", {"position": v(160, 150) * mm});
            skPoint(sketch, "E262.0.2.start.orphan", {"position": v(160, -150) * mm});
            skPoint(sketch, "E265.orphan", {"position": v(-160, -150) * mm});
            skPoint(sketch, "E266.orphan", {"position": v(-160, 150) * mm});
            skPoint(sketch, "E267.0", {"position": v(0, 0) * mm});
            skCircle(sketch, "E268.0", {"center": v(0, 0) * mm, "radius": 4.17 * mm});
            skCircle(sketch, "E269.0", {"center": v(60, 0) * mm, "radius": 5.36 * mm});
            skCircle(sketch, "E270.0", {"center": v(-60, 0) * mm, "radius": 7.13 * mm});
            skSolve(sketch);
        }
        {
            var Q0;
            Q0 = qSketchRegion(id + "F60", true);
            extrude(context, id + "F61", {"entities" : qUnion([Q0]), "oppositeDirection" : true, "depth" : 10 * mm});
        }
    });
